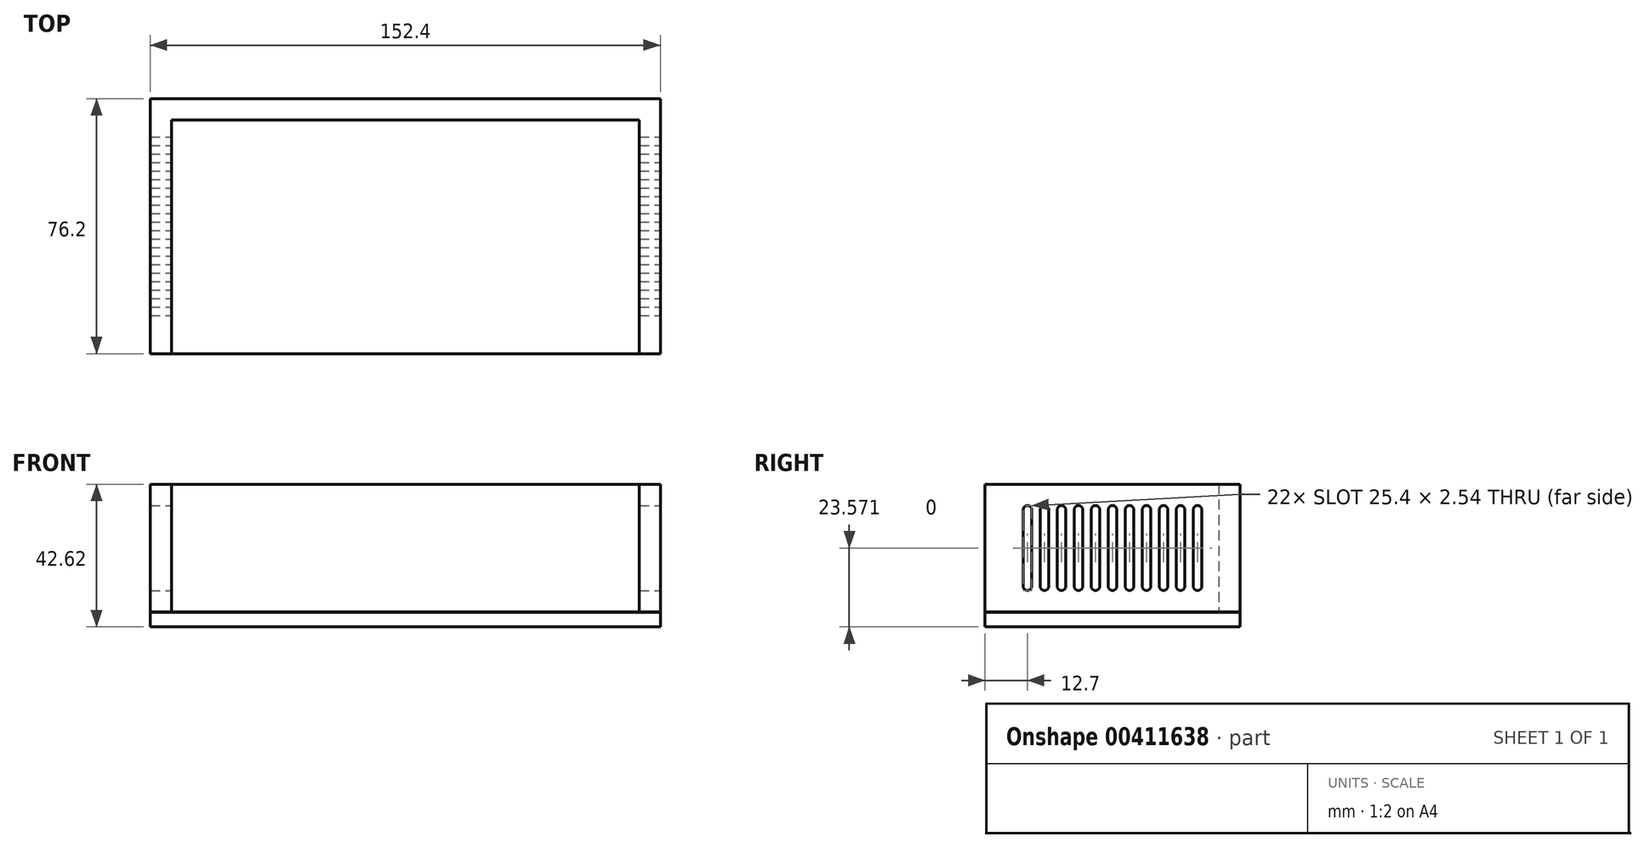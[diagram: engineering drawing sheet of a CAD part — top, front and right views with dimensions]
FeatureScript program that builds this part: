
annotation { "Feature Type Name" : "Feature", "Feature Type Description" : "" }
export const myFeature = defineFeature(function(context is Context, id is Id, definition is map)
    precondition{}
    {
        {
            var Q0;
            Q0=qCreatedBy(makeId("Top.planeOp"),FACE);
            var sketch = newSketch(context, id + "F0", { "sketchPlane" : qUnion([Q0])});
            skLineSegment(sketch, "E0.bottom", {"start": v(0, 0) * mm, "end": v(152.4, 0) * mm});
            skLineSegment(sketch, "E0.top", {"start": v(0, -76.2) * mm, "end": v(152.4, -76.2) * mm});
            skLineSegment(sketch, "E0.left", {"start": v(0, 0) * mm, "end": v(0, -76.2) * mm});
            skLineSegment(sketch, "E0.right", {"start": v(152.4, 0) * mm, "end": v(152.4, -76.2) * mm});
            skSolve(sketch);
        }
        {
            var Q0;
            Q0 = qSketchRegion(id + "F0", true);
            extrude(context, id + "F1", {"entities" : qUnion([Q0]), "depth" : 4.32 * mm});
        }
        {
            var Q0;
            Q0=qCreatedBy(makeId("Top.planeOp"),FACE);
            cPlane(context, id + "F2", {"entities" : qUnion([Q0]), "cplaneType" : CPlaneType.OFFSET, "offset" : 4.52 * mm, "width" : 152.4 * mm, "height" : 152.4 * mm});
        }
        {
            var Q0;
            Q0=qCreatedBy(id+"F2.planeOp",FACE);
            var sketch = newSketch(context, id + "F3", { "sketchPlane" : qUnion([Q0])});
            skLineSegment(sketch, "E1.bottom", {"start": v(0, 0) * mm, "end": v(6.35, 0) * mm});
            skLineSegment(sketch, "E1.top", {"start": v(0, -76.2) * mm, "end": v(6.35, -76.2) * mm});
            skLineSegment(sketch, "E1.left", {"start": v(0, 0) * mm, "end": v(0, -76.2) * mm});
            skLineSegment(sketch, "E1.right", {"start": v(6.35, -6.35) * mm, "end": v(6.35, -76.2) * mm});
            skLineSegment(sketch, "E2.bottom", {"start": v(152.4, 0) * mm, "end": v(146.05, 0) * mm});
            skLineSegment(sketch, "E2.top", {"start": v(152.4, -76.2) * mm, "end": v(146.05, -76.2) * mm});
            skLineSegment(sketch, "E2.left", {"start": v(152.4, 0) * mm, "end": v(152.4, -76.2) * mm});
            skLineSegment(sketch, "E2.right", {"start": v(146.05, -6.35) * mm, "end": v(146.05, -76.2) * mm});
            skLineSegment(sketch, "E3.bottom", {"start": v(6.35, 0) * mm, "end": v(152.4, 0) * mm});
            skLineSegment(sketch, "E3.top", {"start": v(6.35, -6.35) * mm, "end": v(146.05, -6.35) * mm});
            skSolve(sketch);
        }
        {
            var Q0;
            Q0 = qSketchRegion(id + "F3", true);
            extrude(context, id + "F4", {"entities" : qUnion([Q0]), "depth" : 38.1 * mm});
        }
        {
            var Q0;
            Q0=makeQuery(id+"F4.opExtrude","SWEPT_FACE",FACE,{"disambiguationData":[OSD([sQuery(id+"F3.wireOp",EDGE,"E2.left")])]});
            var sketch = newSketch(context, id + "F5", { "sketchPlane" : qUnion([Q0])});
            skLineSegment(sketch, "E4", {"start": v(-6.35, 42.62) * mm, "end": v(-6.35, 0) * mm, "construction": true});
            skLineSegment(sketch, "E5", {"start": v(-69.85, 42.62) * mm, "end": v(-69.85, 4.52) * mm, "construction": true});
            skLineSegment(sketch, "E6", {"start": v(-38.1, 42.62) * mm, "end": v(-38.1, 4.52) * mm, "construction": true});
            skLineSegment(sketch, "E7.bottom", {"start": v(-63.5, 36.27) * mm, "end": v(-63.5, 36.27) * mm});
            skLineSegment(sketch, "E7.top", {"start": v(-63.5, 10.87) * mm, "end": v(-63.5, 10.87) * mm});
            skLineSegment(sketch, "E7.left", {"start": v(-64.77, 35) * mm, "end": v(-64.77, 12.14) * mm});
            skLineSegment(sketch, "E7.right", {"start": v(-62.23, 35) * mm, "end": v(-62.23, 12.14) * mm});
            skPoint(sketch, "E8.visualSharp", {"position": v(-64.77, 36.27) * mm});
            skArc(sketch, "E8.filletArc", {"start": v(-63.5, 36.27) * mm, "mid": v(-64.4, 35.9) * mm, "end": v(-64.77, 35) * mm});
            skPoint(sketch, "E9.visualSharp", {"position": v(-62.23, 36.27) * mm});
            skArc(sketch, "E9.filletArc", {"start": v(-62.23, 35) * mm, "mid": v(-62.6, 35.9) * mm, "end": v(-63.5, 36.27) * mm});
            skPoint(sketch, "E10.visualSharp", {"position": v(-62.23, 10.87) * mm});
            skArc(sketch, "E10.filletArc", {"start": v(-63.5, 10.87) * mm, "mid": v(-62.6, 11.24) * mm, "end": v(-62.23, 12.14) * mm});
            skPoint(sketch, "E11.visualSharp", {"position": v(-64.77, 10.87) * mm});
            skArc(sketch, "E11.filletArc", {"start": v(-64.77, 12.14) * mm, "mid": v(-64.4, 11.24) * mm, "end": v(-63.5, 10.87) * mm});
            skPoint(sketch, "E12.1.0.0", {"position": v(-57.15, 36.27) * mm});
            skPoint(sketch, "E12.1.0.1", {"position": v(-59.7, 36.27) * mm});
            skLineSegment(sketch, "E12.1.0.2", {"start": v(-59.7, 35) * mm, "end": v(-59.7, 12.14) * mm});
            skLineSegment(sketch, "E12.1.0.3", {"start": v(-57.15, 35) * mm, "end": v(-57.15, 12.14) * mm});
            skPoint(sketch, "E12.1.0.4", {"position": v(-59.7, 10.87) * mm});
            skPoint(sketch, "E12.1.0.5", {"position": v(-57.15, 10.87) * mm});
            skArc(sketch, "E12.1.0.6", {"start": v(-57.15, 35) * mm, "mid": v(-57.52, 35.9) * mm, "end": v(-58.42, 36.27) * mm});
            skArc(sketch, "E12.1.0.7", {"start": v(-58.42, 10.87) * mm, "mid": v(-57.52, 11.24) * mm, "end": v(-57.15, 12.14) * mm});
            skArc(sketch, "E12.1.0.8", {"start": v(-59.7, 12.14) * mm, "mid": v(-59.32, 11.24) * mm, "end": v(-58.42, 10.87) * mm});
            skArc(sketch, "E12.1.0.9", {"start": v(-58.42, 36.27) * mm, "mid": v(-59.32, 35.9) * mm, "end": v(-59.7, 35) * mm});
            skPoint(sketch, "E12.2.0.0", {"position": v(-52.07, 36.27) * mm});
            skPoint(sketch, "E12.2.0.1", {"position": v(-54.61, 36.27) * mm});
            skLineSegment(sketch, "E12.2.0.2", {"start": v(-54.61, 35) * mm, "end": v(-54.61, 12.14) * mm});
            skLineSegment(sketch, "E12.2.0.3", {"start": v(-52.07, 35) * mm, "end": v(-52.07, 12.14) * mm});
            skPoint(sketch, "E12.2.0.4", {"position": v(-54.61, 10.87) * mm});
            skPoint(sketch, "E12.2.0.5", {"position": v(-52.07, 10.87) * mm});
            skArc(sketch, "E12.2.0.6", {"start": v(-52.07, 35) * mm, "mid": v(-52.44, 35.9) * mm, "end": v(-53.34, 36.27) * mm});
            skArc(sketch, "E12.2.0.7", {"start": v(-53.34, 10.87) * mm, "mid": v(-52.44, 11.24) * mm, "end": v(-52.07, 12.14) * mm});
            skArc(sketch, "E12.2.0.8", {"start": v(-54.61, 12.14) * mm, "mid": v(-54.24, 11.24) * mm, "end": v(-53.34, 10.87) * mm});
            skArc(sketch, "E12.2.0.9", {"start": v(-53.34, 36.27) * mm, "mid": v(-54.24, 35.9) * mm, "end": v(-54.61, 35) * mm});
            skPoint(sketch, "E12.3.0.0", {"position": v(-47, 36.27) * mm});
            skPoint(sketch, "E12.3.0.1", {"position": v(-49.53, 36.27) * mm});
            skLineSegment(sketch, "E12.3.0.2", {"start": v(-49.53, 35) * mm, "end": v(-49.53, 12.14) * mm});
            skLineSegment(sketch, "E12.3.0.3", {"start": v(-47, 35) * mm, "end": v(-47, 12.14) * mm});
            skPoint(sketch, "E12.3.0.4", {"position": v(-49.53, 10.87) * mm});
            skPoint(sketch, "E12.3.0.5", {"position": v(-47, 10.87) * mm});
            skArc(sketch, "E12.3.0.6", {"start": v(-47, 35) * mm, "mid": v(-47.36, 35.9) * mm, "end": v(-48.26, 36.27) * mm});
            skArc(sketch, "E12.3.0.7", {"start": v(-48.26, 10.87) * mm, "mid": v(-47.36, 11.24) * mm, "end": v(-47, 12.14) * mm});
            skArc(sketch, "E12.3.0.8", {"start": v(-49.53, 12.14) * mm, "mid": v(-49.16, 11.24) * mm, "end": v(-48.26, 10.87) * mm});
            skArc(sketch, "E12.3.0.9", {"start": v(-48.26, 36.27) * mm, "mid": v(-49.16, 35.9) * mm, "end": v(-49.53, 35) * mm});
            skPoint(sketch, "E12.4.0.0", {"position": v(-41.91, 36.27) * mm});
            skPoint(sketch, "E12.4.0.1", {"position": v(-44.45, 36.27) * mm});
            skLineSegment(sketch, "E12.4.0.2", {"start": v(-44.45, 35) * mm, "end": v(-44.45, 12.14) * mm});
            skLineSegment(sketch, "E12.4.0.3", {"start": v(-41.91, 35) * mm, "end": v(-41.91, 12.14) * mm});
            skPoint(sketch, "E12.4.0.4", {"position": v(-44.45, 10.87) * mm});
            skPoint(sketch, "E12.4.0.5", {"position": v(-41.91, 10.87) * mm});
            skArc(sketch, "E12.4.0.6", {"start": v(-41.91, 35) * mm, "mid": v(-42.28, 35.9) * mm, "end": v(-43.18, 36.27) * mm});
            skArc(sketch, "E12.4.0.7", {"start": v(-43.18, 10.87) * mm, "mid": v(-42.28, 11.24) * mm, "end": v(-41.91, 12.14) * mm});
            skArc(sketch, "E12.4.0.8", {"start": v(-44.45, 12.14) * mm, "mid": v(-44.08, 11.24) * mm, "end": v(-43.18, 10.87) * mm});
            skArc(sketch, "E12.4.0.9", {"start": v(-43.18, 36.27) * mm, "mid": v(-44.08, 35.9) * mm, "end": v(-44.45, 35) * mm});
            skPoint(sketch, "E12.5.0.0", {"position": v(-36.83, 36.27) * mm});
            skPoint(sketch, "E12.5.0.1", {"position": v(-39.37, 36.27) * mm});
            skLineSegment(sketch, "E12.5.0.2", {"start": v(-39.37, 35) * mm, "end": v(-39.37, 12.14) * mm});
            skLineSegment(sketch, "E12.5.0.3", {"start": v(-36.83, 35) * mm, "end": v(-36.83, 12.14) * mm});
            skPoint(sketch, "E12.5.0.4", {"position": v(-39.37, 10.87) * mm});
            skPoint(sketch, "E12.5.0.5", {"position": v(-36.83, 10.87) * mm});
            skArc(sketch, "E12.5.0.6", {"start": v(-36.83, 35) * mm, "mid": v(-37.2, 35.9) * mm, "end": v(-38.1, 36.27) * mm});
            skArc(sketch, "E12.5.0.7", {"start": v(-38.1, 10.87) * mm, "mid": v(-37.2, 11.24) * mm, "end": v(-36.83, 12.14) * mm});
            skArc(sketch, "E12.5.0.8", {"start": v(-39.37, 12.14) * mm, "mid": v(-39, 11.24) * mm, "end": v(-38.1, 10.87) * mm});
            skArc(sketch, "E12.5.0.9", {"start": v(-38.1, 36.27) * mm, "mid": v(-39, 35.9) * mm, "end": v(-39.37, 35) * mm});
            skPoint(sketch, "E12.6.0.0", {"position": v(-31.75, 36.27) * mm});
            skPoint(sketch, "E12.6.0.1", {"position": v(-34.3, 36.27) * mm});
            skLineSegment(sketch, "E12.6.0.2", {"start": v(-34.3, 35) * mm, "end": v(-34.3, 12.14) * mm});
            skLineSegment(sketch, "E12.6.0.3", {"start": v(-31.75, 35) * mm, "end": v(-31.75, 12.14) * mm});
            skPoint(sketch, "E12.6.0.4", {"position": v(-34.3, 10.87) * mm});
            skPoint(sketch, "E12.6.0.5", {"position": v(-31.75, 10.87) * mm});
            skArc(sketch, "E12.6.0.6", {"start": v(-31.75, 35) * mm, "mid": v(-32.12, 35.9) * mm, "end": v(-33.02, 36.27) * mm});
            skArc(sketch, "E12.6.0.7", {"start": v(-33.02, 10.87) * mm, "mid": v(-32.12, 11.24) * mm, "end": v(-31.75, 12.14) * mm});
            skArc(sketch, "E12.6.0.8", {"start": v(-34.3, 12.14) * mm, "mid": v(-33.92, 11.24) * mm, "end": v(-33.02, 10.87) * mm});
            skArc(sketch, "E12.6.0.9", {"start": v(-33.02, 36.27) * mm, "mid": v(-33.92, 35.9) * mm, "end": v(-34.3, 35) * mm});
            skPoint(sketch, "E12.7.0.0", {"position": v(-26.67, 36.27) * mm});
            skPoint(sketch, "E12.7.0.1", {"position": v(-29.21, 36.27) * mm});
            skLineSegment(sketch, "E12.7.0.2", {"start": v(-29.21, 35) * mm, "end": v(-29.21, 12.14) * mm});
            skLineSegment(sketch, "E12.7.0.3", {"start": v(-26.67, 35) * mm, "end": v(-26.67, 12.14) * mm});
            skPoint(sketch, "E12.7.0.4", {"position": v(-29.21, 10.87) * mm});
            skPoint(sketch, "E12.7.0.5", {"position": v(-26.67, 10.87) * mm});
            skArc(sketch, "E12.7.0.6", {"start": v(-26.67, 35) * mm, "mid": v(-27.04, 35.9) * mm, "end": v(-27.94, 36.27) * mm});
            skArc(sketch, "E12.7.0.7", {"start": v(-27.94, 10.87) * mm, "mid": v(-27.04, 11.24) * mm, "end": v(-26.67, 12.14) * mm});
            skArc(sketch, "E12.7.0.8", {"start": v(-29.21, 12.14) * mm, "mid": v(-28.84, 11.24) * mm, "end": v(-27.94, 10.87) * mm});
            skArc(sketch, "E12.7.0.9", {"start": v(-27.94, 36.27) * mm, "mid": v(-28.84, 35.9) * mm, "end": v(-29.21, 35) * mm});
            skPoint(sketch, "E12.8.0.0", {"position": v(-21.6, 36.27) * mm});
            skPoint(sketch, "E12.8.0.1", {"position": v(-24.13, 36.27) * mm});
            skLineSegment(sketch, "E12.8.0.2", {"start": v(-24.13, 35) * mm, "end": v(-24.13, 12.14) * mm});
            skLineSegment(sketch, "E12.8.0.3", {"start": v(-21.6, 35) * mm, "end": v(-21.6, 12.14) * mm});
            skPoint(sketch, "E12.8.0.4", {"position": v(-24.13, 10.87) * mm});
            skPoint(sketch, "E12.8.0.5", {"position": v(-21.6, 10.87) * mm});
            skArc(sketch, "E12.8.0.6", {"start": v(-21.6, 35) * mm, "mid": v(-21.96, 35.9) * mm, "end": v(-22.86, 36.27) * mm});
            skArc(sketch, "E12.8.0.7", {"start": v(-22.86, 10.87) * mm, "mid": v(-21.96, 11.24) * mm, "end": v(-21.6, 12.14) * mm});
            skArc(sketch, "E12.8.0.8", {"start": v(-24.13, 12.14) * mm, "mid": v(-23.76, 11.24) * mm, "end": v(-22.86, 10.87) * mm});
            skArc(sketch, "E12.8.0.9", {"start": v(-22.86, 36.27) * mm, "mid": v(-23.76, 35.9) * mm, "end": v(-24.13, 35) * mm});
            skPoint(sketch, "E12.9.0.0", {"position": v(-16.51, 36.27) * mm});
            skPoint(sketch, "E12.9.0.1", {"position": v(-19.05, 36.27) * mm});
            skLineSegment(sketch, "E12.9.0.2", {"start": v(-19.05, 35) * mm, "end": v(-19.05, 12.14) * mm});
            skLineSegment(sketch, "E12.9.0.3", {"start": v(-16.51, 35) * mm, "end": v(-16.51, 12.14) * mm});
            skPoint(sketch, "E12.9.0.4", {"position": v(-19.05, 10.87) * mm});
            skPoint(sketch, "E12.9.0.5", {"position": v(-16.51, 10.87) * mm});
            skArc(sketch, "E12.9.0.6", {"start": v(-16.51, 35) * mm, "mid": v(-16.88, 35.9) * mm, "end": v(-17.78, 36.27) * mm});
            skArc(sketch, "E12.9.0.7", {"start": v(-17.78, 10.87) * mm, "mid": v(-16.88, 11.24) * mm, "end": v(-16.51, 12.14) * mm});
            skArc(sketch, "E12.9.0.8", {"start": v(-19.05, 12.14) * mm, "mid": v(-18.68, 11.24) * mm, "end": v(-17.78, 10.87) * mm});
            skArc(sketch, "E12.9.0.9", {"start": v(-17.78, 36.27) * mm, "mid": v(-18.68, 35.9) * mm, "end": v(-19.05, 35) * mm});
            skPoint(sketch, "E12.10.0.0", {"position": v(-11.43, 36.27) * mm});
            skPoint(sketch, "E12.10.0.1", {"position": v(-13.97, 36.27) * mm});
            skLineSegment(sketch, "E12.10.0.2", {"start": v(-13.97, 35) * mm, "end": v(-13.97, 12.14) * mm});
            skLineSegment(sketch, "E12.10.0.3", {"start": v(-11.43, 35) * mm, "end": v(-11.43, 12.14) * mm});
            skPoint(sketch, "E12.10.0.4", {"position": v(-13.97, 10.87) * mm});
            skPoint(sketch, "E12.10.0.5", {"position": v(-11.43, 10.87) * mm});
            skArc(sketch, "E12.10.0.6", {"start": v(-11.43, 35) * mm, "mid": v(-11.8, 35.9) * mm, "end": v(-12.7, 36.27) * mm});
            skArc(sketch, "E12.10.0.7", {"start": v(-12.7, 10.87) * mm, "mid": v(-11.8, 11.24) * mm, "end": v(-11.43, 12.14) * mm});
            skArc(sketch, "E12.10.0.8", {"start": v(-13.97, 12.14) * mm, "mid": v(-13.6, 11.24) * mm, "end": v(-12.7, 10.87) * mm});
            skArc(sketch, "E12.10.0.9", {"start": v(-12.7, 36.27) * mm, "mid": v(-13.6, 35.9) * mm, "end": v(-13.97, 35) * mm});
            skLineSegment(sketch, "E12.direction1", {"start": v(-64.77, 10.87) * mm, "end": v(-59.7, 10.87) * mm, "construction": true});
            skSolve(sketch);
        }
        {
            var Q0;
            Q0 = qSketchRegion(id + "F5", true);
            extrude(context, id + "F6", {"entities" : qUnion([Q0]), "operationType" : NewBodyOperationType.REMOVE, "oppositeDirection" : true, "depth" : 162.05 * mm});
        }
    });
